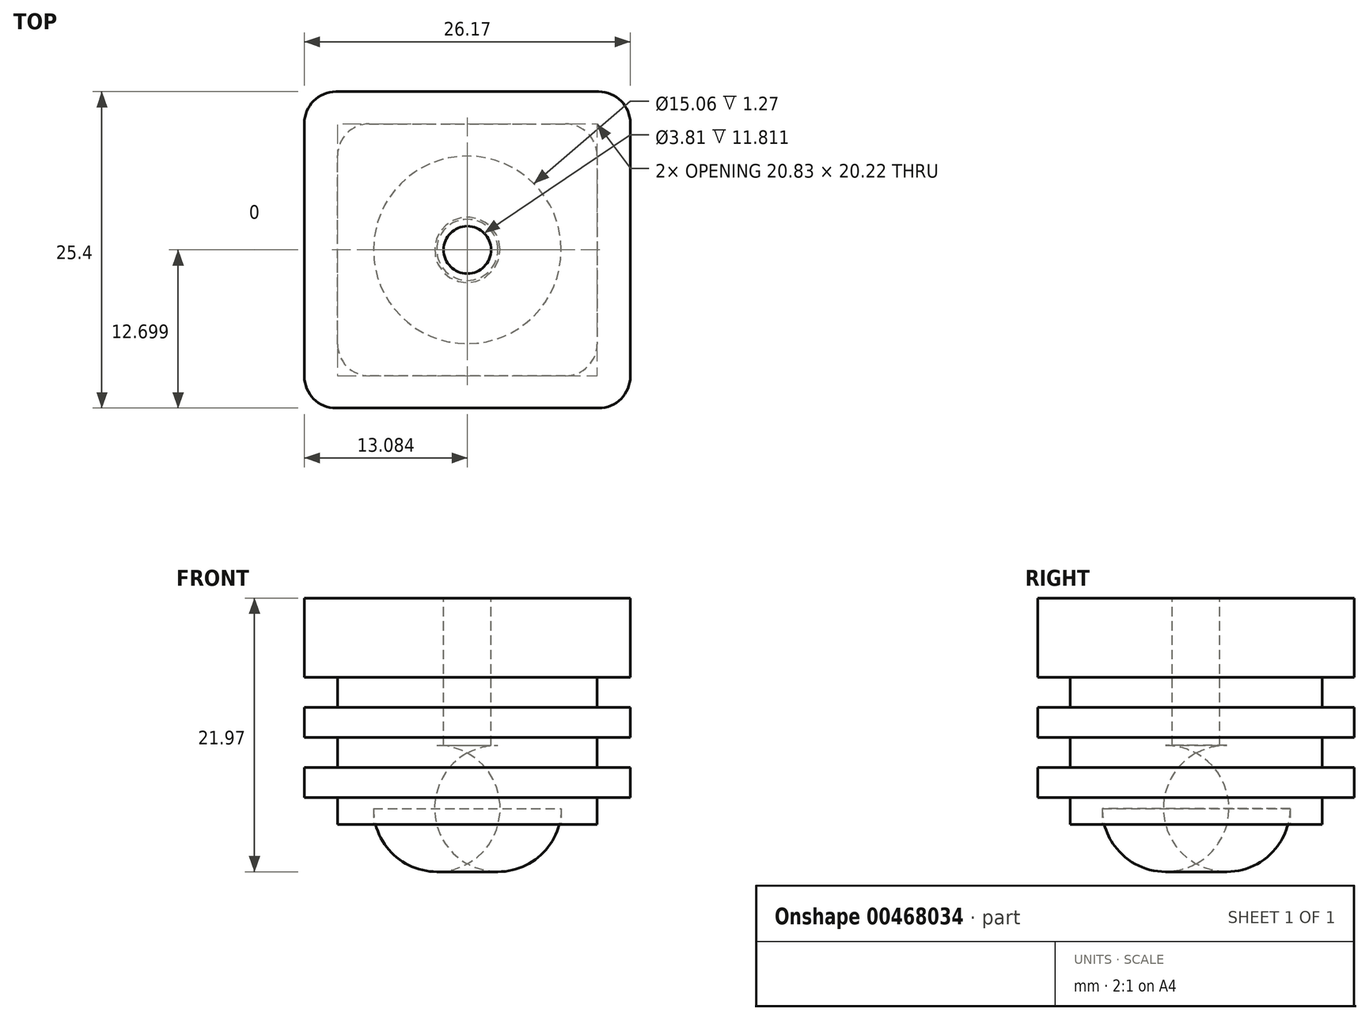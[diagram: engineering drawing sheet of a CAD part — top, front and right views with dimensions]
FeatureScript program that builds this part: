
annotation { "Feature Type Name" : "Feature", "Feature Type Description" : "" }
export const myFeature = defineFeature(function(context is Context, id is Id, definition is map)
    precondition{}
    {
        {
            var Q0;
            Q0=qCreatedBy(makeId("Top.planeOp"),FACE);
            var sketch = newSketch(context, id + "F0", { "sketchPlane" : qUnion([Q0])});
            skLineSegment(sketch, "E0.bottom", {"start": v(2.54, 20.22) * mm, "end": v(18.29, 20.22) * mm});
            skLineSegment(sketch, "E0.top", {"start": v(2.54, 0) * mm, "end": v(18.29, 0) * mm});
            skLineSegment(sketch, "E0.left", {"start": v(0, 17.68) * mm, "end": v(0, 2.54) * mm});
            skLineSegment(sketch, "E0.right", {"start": v(20.83, 17.68) * mm, "end": v(20.83, 2.54) * mm});
            skPoint(sketch, "E1.visualSharp", {"position": v(0, 20.22) * mm});
            skArc(sketch, "E1.filletArc", {"start": v(2.54, 20.22) * mm, "mid": v(0.74, 19.47) * mm, "end": v(0, 17.68) * mm});
            skPoint(sketch, "E2.visualSharp", {"position": v(20.83, 20.22) * mm});
            skArc(sketch, "E2.filletArc", {"start": v(20.83, 17.68) * mm, "mid": v(20.08, 19.47) * mm, "end": v(18.29, 20.22) * mm});
            skPoint(sketch, "E3.visualSharp", {"position": v(20.83, 0) * mm});
            skArc(sketch, "E3.filletArc", {"start": v(18.29, 0) * mm, "mid": v(20.08, 0.74) * mm, "end": v(20.83, 2.54) * mm});
            skPoint(sketch, "E4.visualSharp", {"position": v(0, 0) * mm});
            skArc(sketch, "E4.filletArc", {"start": v(0, 2.54) * mm, "mid": v(0.74, 0.74) * mm, "end": v(2.54, 0) * mm});
            skSolve(sketch);
        }
        {
            var Q0;
            Q0=makeQuery(id+"F0.imprint","IMPRINT",FACE,{"disambiguationData":[TD([[makeQuery(id+"F0.imprint","IMPRINT",EDGE,{"derivedFrom":sQuery(id+"F0.wireOp",EDGE,"E0.bottom")}),-1.0]])]});
            extrude(context, id + "F1", {"entities" : qUnion([Q0]), "depth" : 2.16 * mm, "offsetDistance" : 25.4 * mm});
        }
        {
            var Q0;
            Q0=makeQuery(id+"F1.opExtrude","CAP_FACE",FACE,{"disambiguationData":[OSD([sQuery(id+"F0.wireOp",EDGE,"E0.bottom"),sQuery(id+"F0.wireOp",EDGE,"E0.top"),sQuery(id+"F0.wireOp",EDGE,"E0.left"),sQuery(id+"F0.wireOp",EDGE,"E0.right"),sQuery(id+"F0.wireOp",EDGE,"E1.filletArc"),sQuery(id+"F0.wireOp",EDGE,"E2.filletArc"),sQuery(id+"F0.wireOp",EDGE,"E3.filletArc"),sQuery(id+"F0.wireOp",EDGE,"E4.filletArc")])],"isStart":false});
            var sketch = newSketch(context, id + "F2", { "sketchPlane" : qUnion([Q0])});
            skLineSegment(sketch, "E5.bottom", {"start": v(-0.13, 22.8) * mm, "end": v(20.96, 22.8) * mm});
            skLineSegment(sketch, "E5.top", {"start": v(-0.13, -2.6) * mm, "end": v(20.96, -2.6) * mm});
            skLineSegment(sketch, "E5.left", {"start": v(-2.67, 20.27) * mm, "end": v(-2.67, -0.05) * mm});
            skLineSegment(sketch, "E5.right", {"start": v(23.5, 20.27) * mm, "end": v(23.5, -0.05) * mm});
            skLineSegment(sketch, "E6", {"start": v(10.41, 20.22) * mm, "end": v(10.41, 22.8) * mm, "construction": true});
            skLineSegment(sketch, "E7", {"start": v(10.41, -2.6) * mm, "end": v(10.41, 0) * mm, "construction": true});
            skLineSegment(sketch, "E8", {"start": v(0, 10.1) * mm, "end": v(-2.67, 10.1) * mm, "construction": true});
            skLineSegment(sketch, "E9", {"start": v(20.83, 10.1) * mm, "end": v(23.5, 10.1) * mm, "construction": true});
            skPoint(sketch, "E10.visualSharp", {"position": v(-2.67, 22.8) * mm});
            skArc(sketch, "E10.filletArc", {"start": v(-0.13, 22.8) * mm, "mid": v(-1.92, 22.07) * mm, "end": v(-2.67, 20.27) * mm});
            skPoint(sketch, "E11.visualSharp", {"position": v(-2.67, -2.6) * mm});
            skArc(sketch, "E11.filletArc", {"start": v(-2.67, -0.05) * mm, "mid": v(-1.92, -1.85) * mm, "end": v(-0.13, -2.6) * mm});
            skPoint(sketch, "E12.visualSharp", {"position": v(23.5, -2.6) * mm});
            skArc(sketch, "E12.filletArc", {"start": v(20.96, -2.6) * mm, "mid": v(22.75, -1.85) * mm, "end": v(23.5, -0.05) * mm});
            skPoint(sketch, "E13.visualSharp", {"position": v(23.5, 22.8) * mm});
            skArc(sketch, "E13.filletArc", {"start": v(23.5, 20.27) * mm, "mid": v(22.75, 22.07) * mm, "end": v(20.96, 22.8) * mm});
            skSolve(sketch);
        }
        {
            var Q0;
            Q0 = qSketchRegion(id + "F2", true);
            extrude(context, id + "F3", {"entities" : qUnion([Q0]), "operationType" : NewBodyOperationType.ADD, "depth" : 2.41 * mm});
        }
        {
            var Q0;
            Q0=makeQuery(id+"F3.opExtrude","CAP_FACE",FACE,{"disambiguationData":[OSD([sQuery(id+"F2.wireOp",EDGE,"E5.bottom"),sQuery(id+"F2.wireOp",EDGE,"E5.top"),sQuery(id+"F2.wireOp",EDGE,"E5.left"),sQuery(id+"F2.wireOp",EDGE,"E5.right"),sQuery(id+"F2.wireOp",EDGE,"E10.filletArc"),sQuery(id+"F2.wireOp",EDGE,"E11.filletArc"),sQuery(id+"F2.wireOp",EDGE,"E12.filletArc"),sQuery(id+"F2.wireOp",EDGE,"E13.filletArc")])],"isStart":false});
            var sketch = newSketch(context, id + "F4", { "sketchPlane" : qUnion([Q0])});
            skArc(sketch, "E14.0.0", {"start": v(2.54, 0) * mm, "mid": v(0.74, 0.74) * mm, "end": v(0, 2.54) * mm});
            skLineSegment(sketch, "E14.0.1", {"start": v(0, 2.54) * mm, "end": v(0, 17.68) * mm});
            skArc(sketch, "E14.0.2", {"start": v(0, 17.68) * mm, "mid": v(0.74, 19.47) * mm, "end": v(2.54, 20.22) * mm});
            skLineSegment(sketch, "E14.0.3", {"start": v(2.54, 20.22) * mm, "end": v(18.29, 20.22) * mm});
            skArc(sketch, "E14.0.4", {"start": v(18.29, 20.22) * mm, "mid": v(20.08, 19.47) * mm, "end": v(20.83, 17.68) * mm});
            skLineSegment(sketch, "E14.0.5", {"start": v(20.83, 17.68) * mm, "end": v(20.83, 2.54) * mm});
            skArc(sketch, "E14.0.6", {"start": v(20.83, 2.54) * mm, "mid": v(20.08, 0.74) * mm, "end": v(18.29, 0) * mm});
            skLineSegment(sketch, "E14.0.7", {"start": v(18.29, 0) * mm, "end": v(2.54, 0) * mm});
            skSolve(sketch);
        }
        {
            var Q0;
            Q0 = qSketchRegion(id + "F4", true);
            extrude(context, id + "F5", {"entities" : qUnion([Q0]), "operationType" : NewBodyOperationType.ADD, "depth" : 2.41 * mm});
        }
        {
            var Q0;
            Q0=makeQuery(id+"F5.opExtrude","CAP_FACE",FACE,{"disambiguationData":[OSD([sQuery(id+"F4.wireOp",EDGE,"E14.0.0"),sQuery(id+"F4.wireOp",EDGE,"E14.0.1"),sQuery(id+"F4.wireOp",EDGE,"E14.0.2"),sQuery(id+"F4.wireOp",EDGE,"E14.0.3"),sQuery(id+"F4.wireOp",EDGE,"E14.0.4"),sQuery(id+"F4.wireOp",EDGE,"E14.0.5"),sQuery(id+"F4.wireOp",EDGE,"E14.0.6"),sQuery(id+"F4.wireOp",EDGE,"E14.0.7")])],"isStart":false});
            var sketch = newSketch(context, id + "F6", { "sketchPlane" : qUnion([Q0])});
            skArc(sketch, "E15.0.0", {"start": v(-2.67, -0.05) * mm, "mid": v(-1.92, -1.85) * mm, "end": v(-0.13, -2.6) * mm});
            skLineSegment(sketch, "E15.0.1", {"start": v(-0.13, -2.6) * mm, "end": v(20.96, -2.6) * mm});
            skArc(sketch, "E15.0.2", {"start": v(20.96, -2.6) * mm, "mid": v(22.75, -1.85) * mm, "end": v(23.5, -0.05) * mm});
            skLineSegment(sketch, "E15.0.3", {"start": v(23.5, -0.05) * mm, "end": v(23.5, 20.27) * mm});
            skArc(sketch, "E15.0.4", {"start": v(23.5, 20.27) * mm, "mid": v(22.75, 22.07) * mm, "end": v(20.96, 22.8) * mm});
            skLineSegment(sketch, "E15.0.5", {"start": v(20.96, 22.8) * mm, "end": v(-0.13, 22.8) * mm});
            skArc(sketch, "E15.0.6", {"start": v(-0.13, 22.8) * mm, "mid": v(-1.92, 22.07) * mm, "end": v(-2.67, 20.27) * mm});
            skLineSegment(sketch, "E15.0.7", {"start": v(-2.67, 20.27) * mm, "end": v(-2.67, -0.05) * mm});
            skSolve(sketch);
        }
        {
            var Q0;
            Q0 = qSketchRegion(id + "F6", true);
            extrude(context, id + "F7", {"entities" : qUnion([Q0]), "operationType" : NewBodyOperationType.ADD, "depth" : 2.41 * mm});
        }
        {
            var Q0;
            Q0=makeQuery(id+"F7.opExtrude","CAP_FACE",FACE,{"disambiguationData":[OSD([sQuery(id+"F6.wireOp",EDGE,"E15.0.0"),sQuery(id+"F6.wireOp",EDGE,"E15.0.1"),sQuery(id+"F6.wireOp",EDGE,"E15.0.2"),sQuery(id+"F6.wireOp",EDGE,"E15.0.3"),sQuery(id+"F6.wireOp",EDGE,"E15.0.4"),sQuery(id+"F6.wireOp",EDGE,"E15.0.5"),sQuery(id+"F6.wireOp",EDGE,"E15.0.6"),sQuery(id+"F6.wireOp",EDGE,"E15.0.7")])],"isStart":false});
            var sketch = newSketch(context, id + "F8", { "sketchPlane" : qUnion([Q0])});
            skArc(sketch, "E16.0.0", {"start": v(2.54, 0) * mm, "mid": v(0.74, 0.74) * mm, "end": v(0, 2.54) * mm});
            skLineSegment(sketch, "E16.0.1", {"start": v(0, 2.54) * mm, "end": v(0, 17.68) * mm});
            skArc(sketch, "E16.0.2", {"start": v(0, 17.68) * mm, "mid": v(0.74, 19.47) * mm, "end": v(2.54, 20.22) * mm});
            skLineSegment(sketch, "E16.0.3", {"start": v(2.54, 20.22) * mm, "end": v(18.29, 20.22) * mm});
            skArc(sketch, "E16.0.4", {"start": v(18.29, 20.22) * mm, "mid": v(20.08, 19.47) * mm, "end": v(20.83, 17.68) * mm});
            skLineSegment(sketch, "E16.0.5", {"start": v(20.83, 17.68) * mm, "end": v(20.83, 2.54) * mm});
            skArc(sketch, "E16.0.6", {"start": v(20.83, 2.54) * mm, "mid": v(20.08, 0.74) * mm, "end": v(18.29, 0) * mm});
            skLineSegment(sketch, "E16.0.7", {"start": v(18.29, 0) * mm, "end": v(2.54, 0) * mm});
            skSolve(sketch);
        }
        {
            var Q0;
            Q0 = qSketchRegion(id + "F8", true);
            extrude(context, id + "F9", {"entities" : qUnion([Q0]), "operationType" : NewBodyOperationType.ADD, "depth" : 2.41 * mm});
        }
        {
            var Q0;
            Q0=makeQuery(id+"F9.opExtrude","CAP_FACE",FACE,{"disambiguationData":[OSD([sQuery(id+"F8.wireOp",EDGE,"E16.0.0"),sQuery(id+"F8.wireOp",EDGE,"E16.0.1"),sQuery(id+"F8.wireOp",EDGE,"E16.0.2"),sQuery(id+"F8.wireOp",EDGE,"E16.0.3"),sQuery(id+"F8.wireOp",EDGE,"E16.0.4"),sQuery(id+"F8.wireOp",EDGE,"E16.0.5"),sQuery(id+"F8.wireOp",EDGE,"E16.0.6"),sQuery(id+"F8.wireOp",EDGE,"E16.0.7")])],"isStart":false});
            var sketch = newSketch(context, id + "F10", { "sketchPlane" : qUnion([Q0])});
            skArc(sketch, "E17.0.0", {"start": v(-0.13, 22.8) * mm, "mid": v(-1.92, 22.07) * mm, "end": v(-2.67, 20.27) * mm});
            skLineSegment(sketch, "E17.0.1", {"start": v(-2.67, 20.27) * mm, "end": v(-2.67, -0.05) * mm});
            skArc(sketch, "E17.0.2", {"start": v(-2.67, -0.05) * mm, "mid": v(-1.92, -1.85) * mm, "end": v(-0.13, -2.6) * mm});
            skLineSegment(sketch, "E17.0.3", {"start": v(-0.13, -2.6) * mm, "end": v(20.96, -2.6) * mm});
            skArc(sketch, "E17.0.4", {"start": v(20.96, -2.6) * mm, "mid": v(22.75, -1.85) * mm, "end": v(23.5, -0.05) * mm});
            skLineSegment(sketch, "E17.0.5", {"start": v(23.5, -0.05) * mm, "end": v(23.5, 20.27) * mm});
            skArc(sketch, "E17.0.6", {"start": v(23.5, 20.27) * mm, "mid": v(22.75, 22.07) * mm, "end": v(20.96, 22.8) * mm});
            skLineSegment(sketch, "E17.0.7", {"start": v(20.96, 22.8) * mm, "end": v(-0.13, 22.8) * mm});
            skSolve(sketch);
        }
        {
            var Q0;
            Q0 = qSketchRegion(id + "F10", true);
            extrude(context, id + "F11", {"entities" : qUnion([Q0]), "operationType" : NewBodyOperationType.ADD, "depth" : 6.35 * mm});
        }
        {
            var Q0;
            Q0=makeQuery(id+"F11.opExtrude","SWEPT_FACE",FACE,{"disambiguationData":[OSD([sQuery(id+"F10.wireOp",EDGE,"E17.0.3")])]});
            cPlane(context, id + "F12", {"entities" : qUnion([Q0]), "cplaneType" : CPlaneType.OFFSET, "offset" : 12.7 * mm, "oppositeDirection" : true, "width" : 152.4 * mm, "height" : 152.4 * mm});
        }
        {
            var Q0;
            Q0=qCreatedBy(id+"F12.planeOp",FACE);
            var sketch = newSketch(context, id + "F13", { "sketchPlane" : qUnion([Q0])});
            skArc(sketch, "E18", {"start": v(17.95, -3.18) * mm, "mid": v(10.41, 4.36) * mm, "end": v(2.88, -3.17) * mm});
            skLineSegment(sketch, "E19", {"start": v(10.41, -3.18) * mm, "end": v(10.41, 0) * mm, "construction": true});
            skLineSegment(sketch, "E20", {"start": v(2.88, -3.18) * mm, "end": v(17.95, -3.18) * mm, "construction": true});
            skSolve(sketch);
        }
        {
            var Q0;
            Q0=makeQuery(id+"F1.opExtrude","CAP_FACE",FACE,{"disambiguationData":[OSD([sQuery(id+"F0.wireOp",EDGE,"E0.bottom"),sQuery(id+"F0.wireOp",EDGE,"E0.top"),sQuery(id+"F0.wireOp",EDGE,"E0.left"),sQuery(id+"F0.wireOp",EDGE,"E0.right"),sQuery(id+"F0.wireOp",EDGE,"E1.filletArc"),sQuery(id+"F0.wireOp",EDGE,"E2.filletArc"),sQuery(id+"F0.wireOp",EDGE,"E3.filletArc"),sQuery(id+"F0.wireOp",EDGE,"E4.filletArc")])],"isStart":true});
            var sketch = newSketch(context, id + "F14", { "sketchPlane" : qUnion([Q0])});
            skCircle(sketch, "E21", {"center": v(10.41, -10.1) * mm, "radius": 7.53 * mm});
            skLineSegment(sketch, "E22", {"start": v(10.41, 0) * mm, "end": v(10.41, -20.22) * mm, "construction": true});
            skSolve(sketch);
        }
        {
            var Q0;
            Q0 = qSketchRegion(id + "F14", true);
            extrude(context, id + "F15", {"entities" : qUnion([Q0]), "operationType" : NewBodyOperationType.REMOVE, "oppositeDirection" : true, "depth" : 6.35 * mm});
        }
        {
            var Q0;
            Q0=makeQuery(id+"F15.boolean.opBoolean","COPY",EDGE,{"derivedFrom":makeQuery(id+"F15.opExtrude","CAP_EDGE",EDGE,{"disambiguationData":[OSD([sQuery(id+"F14.wireOp",EDGE,"E21")])],"isStart":false})});
            fillet(context, id + "F16", {"entities" : qUnion([Q0]), "radius" : 5.08 * mm, "tangentPropagation" : true, "defaultsChanged" : false, "allowEdgeOverflow" : false, "vertexSettings" : [], "filletType" : FilletType.EDGE});
        }
        {
            var Q0;
            Q0=makeQuery(id+"F11.opExtrude","CAP_FACE",FACE,{"disambiguationData":[OSD([sQuery(id+"F10.wireOp",EDGE,"E17.0.0"),sQuery(id+"F10.wireOp",EDGE,"E17.0.1"),sQuery(id+"F10.wireOp",EDGE,"E17.0.2"),sQuery(id+"F10.wireOp",EDGE,"E17.0.3"),sQuery(id+"F10.wireOp",EDGE,"E17.0.4"),sQuery(id+"F10.wireOp",EDGE,"E17.0.5"),sQuery(id+"F10.wireOp",EDGE,"E17.0.6"),sQuery(id+"F10.wireOp",EDGE,"E17.0.7")])],"isStart":false});
            var sketch = newSketch(context, id + "F17", { "sketchPlane" : qUnion([Q0])});
            skCircle(sketch, "E23", {"center": v(10.41, 10.1) * mm, "radius": 1.9 * mm});
            skSolve(sketch);
        }
        {
            var Q0;
            Q0 = qSketchRegion(id + "F17", true);
            extrude(context, id + "F18", {"entities" : qUnion([Q0]), "operationType" : NewBodyOperationType.REMOVE, "endBound" : BoundingType.THROUGH_ALL, "oppositeDirection" : true, "depth" : 25.4 * mm});
        }
    });
